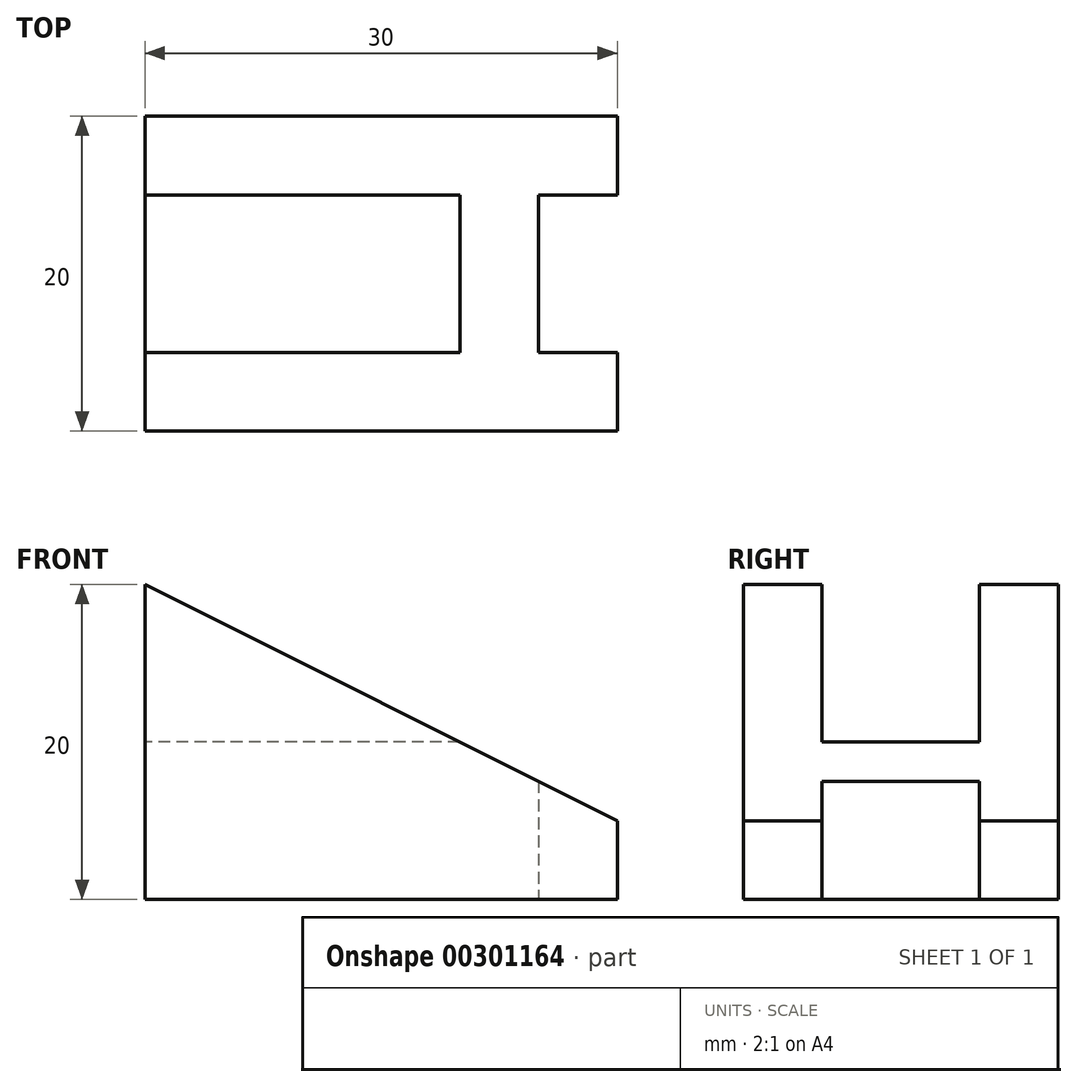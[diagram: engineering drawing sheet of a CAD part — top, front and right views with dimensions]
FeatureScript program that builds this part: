
annotation { "Feature Type Name" : "Feature", "Feature Type Description" : "" }
export const myFeature = defineFeature(function(context is Context, id is Id, definition is map)
    precondition{}
    {
        {
            var Q0;
            Q0=qCreatedBy(makeId("Front.planeOp"),FACE);
            var sketch = newSketch(context, id + "F0", { "sketchPlane" : qUnion([Q0])});
            skLineSegment(sketch, "E0", {"start": v(0, 0) * mm, "end": v(0, 20) * mm});
            skLineSegment(sketch, "E1", {"start": v(0, 0) * mm, "end": v(30, 0) * mm});
            skLineSegment(sketch, "E2", {"start": v(30, 0) * mm, "end": v(30, 5) * mm});
            skLineSegment(sketch, "E3", {"start": v(30, 5) * mm, "end": v(0, 20) * mm});
            skSolve(sketch);
        }
        {
            var Q0;
            Q0=makeQuery(id+"F0.imprint","IMPRINT",FACE,{"disambiguationData":[TD([[makeQuery(id+"F0.imprint","IMPRINT",EDGE,{"derivedFrom":sQuery(id+"F0.wireOp",EDGE,"E0")}),-1.0]])]});
            extrude(context, id + "F1", {"entities" : qUnion([Q0]), "endBound" : BoundingType.SYMMETRIC, "depth" : 20 * mm});
        }
        {
            var Q0;
            Q0=makeQuery(id+"F1.opExtrude","SWEPT_FACE",FACE,{"disambiguationData":[OSD([sQuery(id+"F0.wireOp",EDGE,"E1")])]});
            var sketch = newSketch(context, id + "F2", { "sketchPlane" : qUnion([Q0])});
            skLineSegment(sketch, "E4", {"start": v(30, 5) * mm, "end": v(25, 5) * mm});
            skLineSegment(sketch, "E5", {"start": v(25, 5) * mm, "end": v(25, -5) * mm});
            skLineSegment(sketch, "E6", {"start": v(25, -5) * mm, "end": v(30, -5) * mm});
            skLineSegment(sketch, "E7", {"start": v(30, 5) * mm, "end": v(30, -5) * mm});
            skSolve(sketch);
        }
        {
            var Q0;
            Q0=makeQuery(id+"F2.imprint","IMPRINT",FACE,{"disambiguationData":[TD([[makeQuery(id+"F2.imprint","IMPRINT",EDGE,{"derivedFrom":sQuery(id+"F2.wireOp",EDGE,"E4")}),1.0]])]});
            extrude(context, id + "F3", {"entities" : qUnion([Q0]), "operationType" : NewBodyOperationType.REMOVE, "endBound" : BoundingType.THROUGH_ALL, "oppositeDirection" : true, "depth" : 25 * mm});
        }
        {
            var Q0;
            Q0=makeQuery(id+"F1.opExtrude","SWEPT_FACE",FACE,{"disambiguationData":[OSD([sQuery(id+"F0.wireOp",EDGE,"E0")])]});
            var sketch = newSketch(context, id + "F4", { "sketchPlane" : qUnion([Q0])});
            skLineSegment(sketch, "E8", {"start": v(-5, 20) * mm, "end": v(-5, 10) * mm});
            skLineSegment(sketch, "E9", {"start": v(-5, 10) * mm, "end": v(5, 10) * mm});
            skLineSegment(sketch, "E10", {"start": v(5, 10) * mm, "end": v(5, 20) * mm});
            skLineSegment(sketch, "E11", {"start": v(5, 20) * mm, "end": v(-5, 20) * mm});
            skSolve(sketch);
        }
        {
            var Q0;
            Q0=makeQuery(id+"F4.imprint","IMPRINT",FACE,{"disambiguationData":[TD([[makeQuery(id+"F4.imprint","IMPRINT",EDGE,{"derivedFrom":sQuery(id+"F4.wireOp",EDGE,"E8")}),1.0]])]});
            extrude(context, id + "F5", {"entities" : qUnion([Q0]), "operationType" : NewBodyOperationType.REMOVE, "endBound" : BoundingType.THROUGH_ALL, "oppositeDirection" : true, "depth" : 25 * mm});
        }
    });
